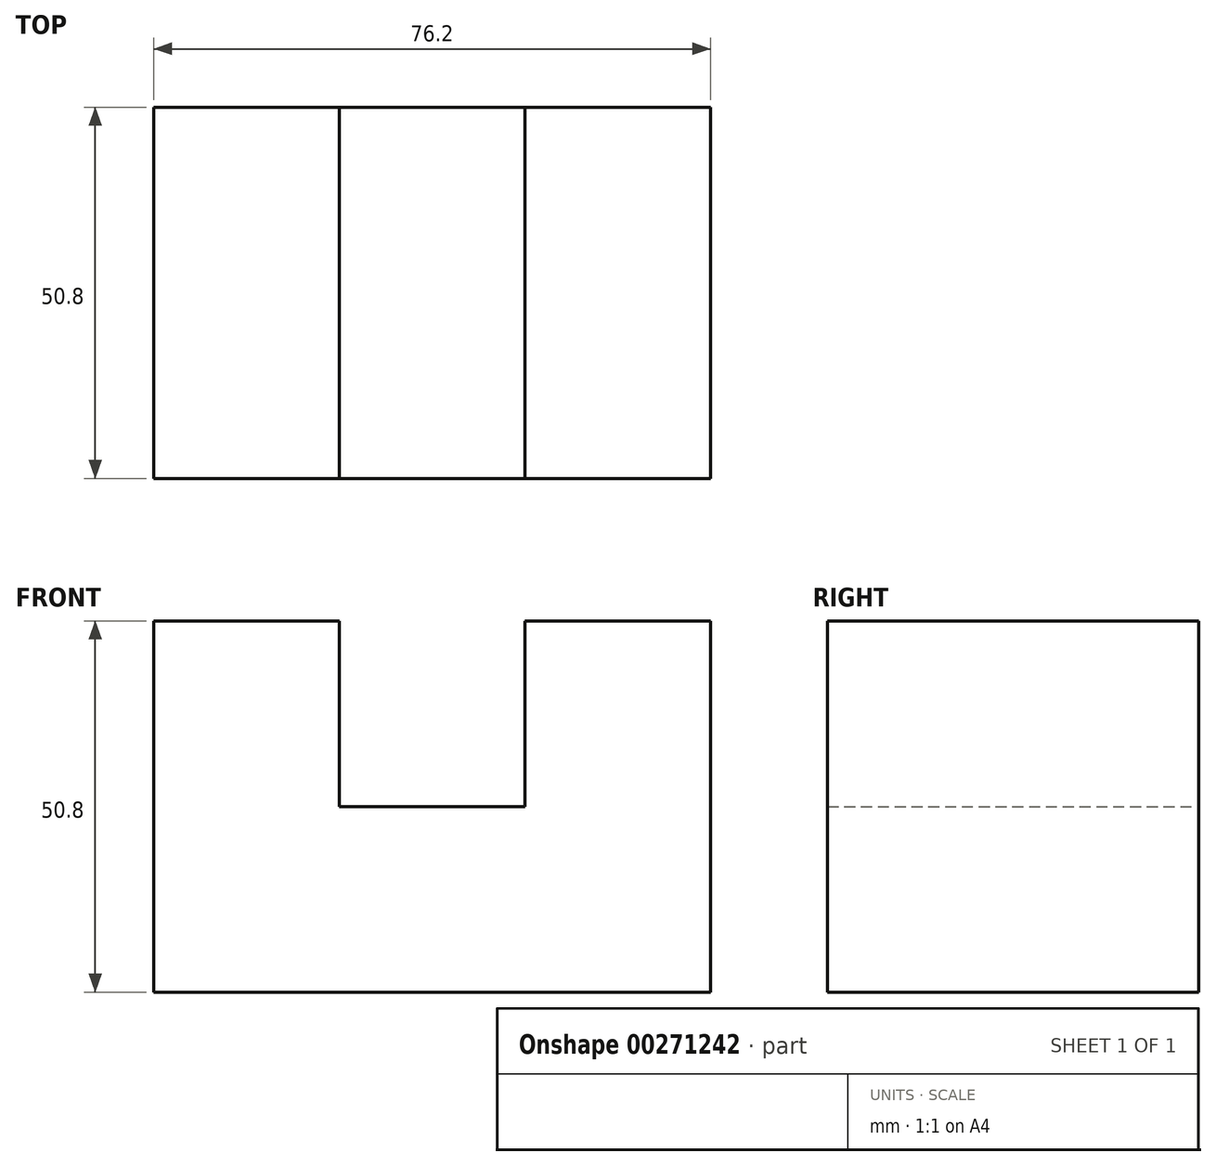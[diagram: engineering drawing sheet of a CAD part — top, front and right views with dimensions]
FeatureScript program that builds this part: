
annotation { "Feature Type Name" : "Feature", "Feature Type Description" : "" }
export const myFeature = defineFeature(function(context is Context, id is Id, definition is map)
    precondition{}
    {
        {
            var Q0;
            Q0=qCreatedBy(makeId("Front.planeOp"),FACE);
            var sketch = newSketch(context, id + "F0", { "sketchPlane" : qUnion([Q0])});
            skLineSegment(sketch, "E0", {"start": v(-50.41, 0) * mm, "end": v(-50.41, 50.8) * mm});
            skLineSegment(sketch, "E1", {"start": v(-50.41, 50.8) * mm, "end": v(-25.01, 50.8) * mm});
            skLineSegment(sketch, "E2", {"start": v(-25.01, 50.8) * mm, "end": v(-25.01, 25.4) * mm});
            skLineSegment(sketch, "E3", {"start": v(-25.01, 25.4) * mm, "end": v(0.39, 25.4) * mm});
            skLineSegment(sketch, "E4", {"start": v(0.39, 25.4) * mm, "end": v(0.39, 50.8) * mm});
            skLineSegment(sketch, "E5", {"start": v(0.39, 50.8) * mm, "end": v(25.79, 50.8) * mm});
            skLineSegment(sketch, "E6", {"start": v(25.79, 50.8) * mm, "end": v(25.79, 0) * mm});
            skLineSegment(sketch, "E7", {"start": v(-50.41, 0) * mm, "end": v(25.79, 0) * mm});
            skSolve(sketch);
        }
        {
            var Q0;
            Q0=makeQuery(id+"F0.imprint","IMPRINT",FACE,{"disambiguationData":[TD([[makeQuery(id+"F0.imprint","IMPRINT",EDGE,{"derivedFrom":sQuery(id+"F0.wireOp",EDGE,"E0")}),-1.0]])]});
            extrude(context, id + "F1", {"entities" : qUnion([Q0]), "depth" : 50.8 * mm});
        }
    });
